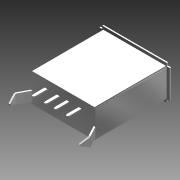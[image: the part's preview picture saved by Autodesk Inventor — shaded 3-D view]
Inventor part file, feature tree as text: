
AUTODESK INVENTOR PART (.ipt)
format: ipt  version: 2014 SP1 (Build 180222100, 222)  size: 187,392 bytes
history: native  units: in
note: dims shown in document units (in); Inventor stores cm internally (conversion verified against a paired STEP export)
features: mirror x1, imported_body x1
ambient origin geometry x8: Origin, YZ Plane, XZ Plane, XY Plane, X Axis, Y Axis, Z Axis, Center Point
bodies: Body1 (feature_tree)
feature tree (2):
  mirror  "Mirror2"
  imported_body  "Base1"
